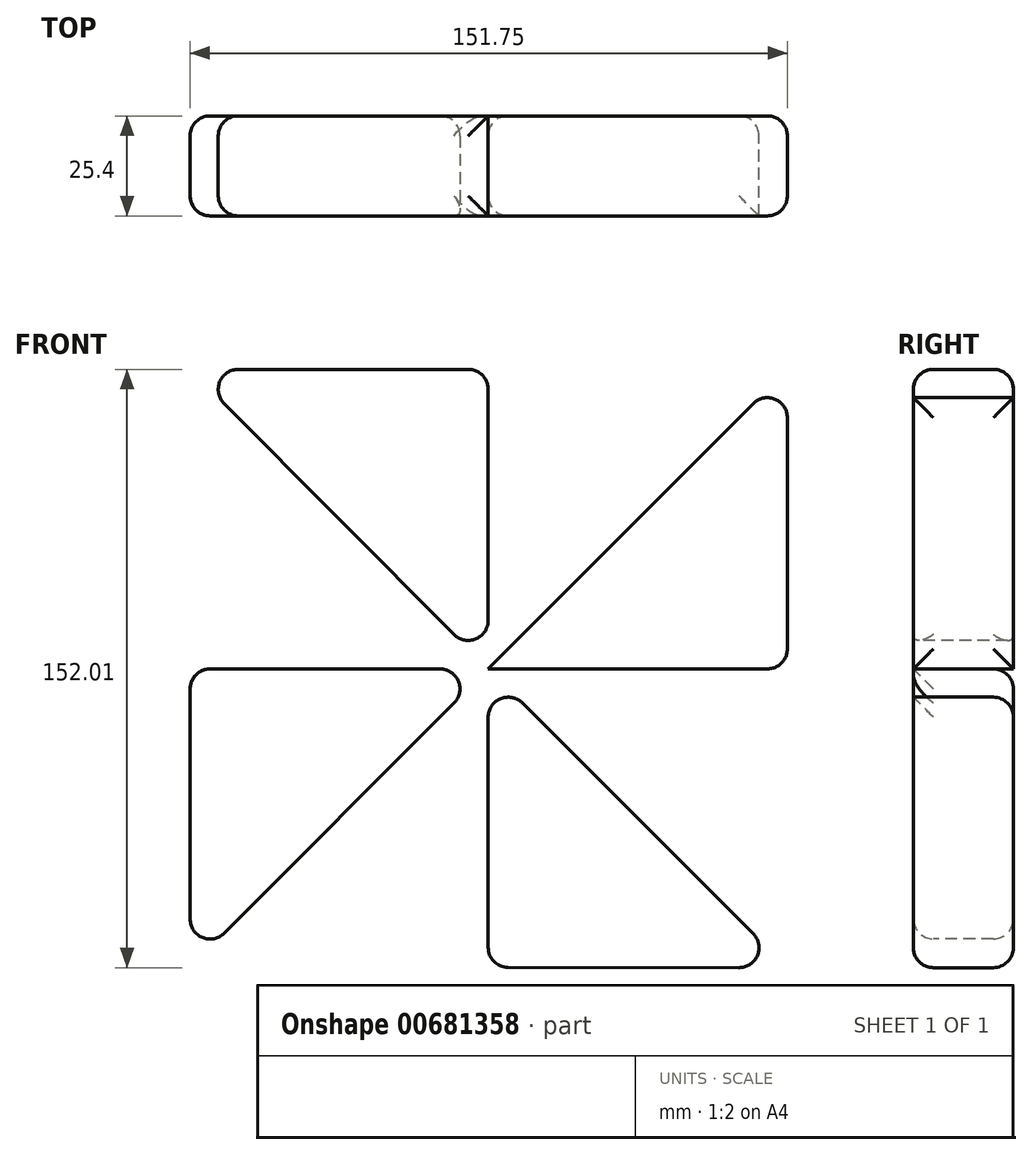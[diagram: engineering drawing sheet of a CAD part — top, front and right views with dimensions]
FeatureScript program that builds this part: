
annotation { "Feature Type Name" : "Feature", "Feature Type Description" : "" }
export const myFeature = defineFeature(function(context is Context, id is Id, definition is map)
    precondition{}
    {
        {
            var Q0;
            Q0=qCreatedBy(makeId("Front.planeOp"),FACE);
            var sketch = newSketch(context, id + "F0", { "sketchPlane" : qUnion([Q0])});
            skLineSegment(sketch, "E0", {"start": v(0, 0) * mm, "end": v(76.02, 76.11) * mm});
            skLineSegment(sketch, "E1", {"start": v(76.02, 76.11) * mm, "end": v(-75.73, -75.83) * mm});
            skLineSegment(sketch, "E2", {"start": v(-75.73, -75.83) * mm, "end": v(0, -75.83) * mm});
            skLineSegment(sketch, "E3", {"start": v(0, -75.83) * mm, "end": v(0, 0) * mm});
            skLineSegment(sketch, "E4", {"start": v(0, 76.11) * mm, "end": v(-75.71, 76.11) * mm});
            skLineSegment(sketch, "E5", {"start": v(-75.71, 76.11) * mm, "end": v(0, 0) * mm});
            skLineSegment(sketch, "E6", {"start": v(0, 0) * mm, "end": v(76.02, -75.92) * mm});
            skLineSegment(sketch, "E7", {"start": v(76.02, -75.92) * mm, "end": v(0, -75.83) * mm});
            skLineSegment(sketch, "E8", {"start": v(0, 76.11) * mm, "end": v(0, 0) * mm});
            skLineSegment(sketch, "E9", {"start": v(0, 76.11) * mm, "end": v(76.02, 76.11) * mm});
            skLineSegment(sketch, "E10", {"start": v(0, 0) * mm, "end": v(76.02, 0) * mm});
            skLineSegment(sketch, "E11", {"start": v(76.02, 0) * mm, "end": v(-75.71, 0) * mm});
            skLineSegment(sketch, "E12", {"start": v(-75.71, 0) * mm, "end": v(-75.73, -75.83) * mm});
            skLineSegment(sketch, "E13", {"start": v(76.02, 0) * mm, "end": v(76.02, -75.92) * mm});
            skLineSegment(sketch, "E14", {"start": v(76.02, 76.11) * mm, "end": v(76.02, 0) * mm});
            skLineSegment(sketch, "E15", {"start": v(-75.71, 76.11) * mm, "end": v(-75.71, 0) * mm});
            skSolve(sketch);
        }
        {
            var Q0;
            Q0=makeQuery(id+"F0.imprint","IMPRINT",FACE,{"disambiguationData":[TD([[makeQuery(id+"F0.imprint","IMPRINT",EDGE,{"derivedFrom":sQuery(id+"F0.wireOp",EDGE,"E3")}),-1.0]])]});
            var Q1;
            Q1=makeQuery(id+"F0.imprint","IMPRINT",FACE,{"disambiguationData":[TD([[makeQuery(id+"F0.imprint","IMPRINT",EDGE,{"derivedFrom":sQuery(id+"F0.wireOp",EDGE,"E4")}),1.0]])]});
            var Q2;
            {var subQ0=sQuery(id+"F0.wireOp",EDGE,"E14");Q2=makeQuery(id+"F0.imprint","IMPRINT",FACE,{"disambiguationData":[TD([[makeQuery(id+"F0.imprint","IMPRINT",EDGE,{"derivedFrom":subQ0}),-1.0]])]});}
            var Q3;
            {var subQ0=sQuery(id+"F0.wireOp",EDGE,"E12");Q3=makeQuery(id+"F0.imprint","IMPRINT",FACE,{"disambiguationData":[TD([[makeQuery(id+"F0.imprint","IMPRINT",EDGE,{"derivedFrom":subQ0}),1.0]])]});}
            extrude(context, id + "F1", {"entities" : qUnion([Q0, Q1, Q2, Q3]), "depth" : 25.4 * mm, "offsetDistance" : 25.4 * mm});
        }
        {
            var Q0;
            Q0=makeQuery(id+"F1.opExtrude","SWEPT_FACE",FACE,{"disambiguationData":[OSD([sQuery(id+"F0.wireOp",EDGE,"E5")])]});
            var Q1;
            Q1=makeQuery(id+"F1.opExtrude","SWEPT_FACE",FACE,{"disambiguationData":[OSD([sQuery(id+"F0.wireOp",EDGE,"E4")])]});
            var Q2;
            Q2=makeQuery(id+"F1.opExtrude","SWEPT_FACE",FACE,{"disambiguationData":[OSD([sQuery(id+"F0.wireOp",EDGE,"E14")])]});
            var Q3;
            {var subQ0=sQuery(id+"F0.wireOp",EDGE,"E1");Q3=makeQuery(id+"F1.opExtrude","SWEPT_FACE",FACE,{"disambiguationData":[OSD([subQ0]),TDD([makeQuery(id+"F0.imprint","IMPRINT",EDGE,{"disambiguationData":[TD([[makeQuery(id+"F0.imprint","INTERSECT",VERTEX,{"derivedFrom":[subQ0,sQuery(id+"F0.wireOp",EDGE,"E9"),sQuery(id+"F0.wireOp",EDGE,"E14")]}),-1.0]])],"derivedFrom":subQ0})])]});}
            var Q4;
            Q4=makeQuery(id+"F1.opExtrude","SWEPT_FACE",FACE,{"disambiguationData":[OSD([sQuery(id+"F0.wireOp",EDGE,"E7")])]});
            var Q5;
            Q5=makeQuery(id+"F1.opExtrude","SWEPT_FACE",FACE,{"disambiguationData":[OSD([sQuery(id+"F0.wireOp",EDGE,"E3")])]});
            var Q6;
            {var subQ0=sQuery(id+"F0.wireOp",EDGE,"E1");Q6=makeQuery(id+"F1.opExtrude","SWEPT_FACE",FACE,{"disambiguationData":[OSD([subQ0]),TDD([makeQuery(id+"F0.imprint","IMPRINT",EDGE,{"disambiguationData":[TD([[makeQuery(id+"F0.imprint","INTERSECT",VERTEX,{"derivedFrom":[subQ0,sQuery(id+"F0.wireOp",EDGE,"E2"),sQuery(id+"F0.wireOp",EDGE,"E12")]}),1.0]])],"derivedFrom":subQ0})])]});}
            var Q7;
            Q7=makeQuery(id+"F1.opExtrude","SWEPT_EDGE",EDGE,{"disambiguationData":[OSD([sQuery(id+"F0.wireOp",EDGE,"E11"),sQuery(id+"F0.wireOp",EDGE,"E12"),sQuery(id+"F0.wireOp",EDGE,"E15")])]});
            var Q8;
            Q8=makeQuery(id+"F1.opExtrude","SWEPT_FACE",FACE,{"disambiguationData":[OSD([sQuery(id+"F0.wireOp",EDGE,"E12")])]});
            var Q9;
            Q9=makeQuery(id+"F1.opExtrude","SWEPT_EDGE",EDGE,{"disambiguationData":[OSD([sQuery(id+"F0.wireOp",EDGE,"E6"),sQuery(id+"F0.wireOp",EDGE,"E7"),sQuery(id+"F0.wireOp",EDGE,"E13")])]});
            var Q10;
            Q10=makeQuery(id+"F1.opExtrude","CAP_EDGE",EDGE,{"disambiguationData":[OSD([sQuery(id+"F0.wireOp",EDGE,"E6")])],"isStart":true});
            var Q11;
            Q11=makeQuery(id+"F1.opExtrude","CAP_EDGE",EDGE,{"disambiguationData":[OSD([sQuery(id+"F0.wireOp",EDGE,"E7")])],"isStart":true});
            var Q12;
            Q12=makeQuery(id+"F1.opExtrude","SWEPT_EDGE",EDGE,{"disambiguationData":[OSD([sQuery(id+"F0.wireOp",EDGE,"E11"),sQuery(id+"F0.wireOp",EDGE,"E13"),sQuery(id+"F0.wireOp",EDGE,"E14")])]});
            var Q13;
            {var subQ0=sQuery(id+"F0.wireOp",EDGE,"E11");Q13=makeQuery(id+"F1.opExtrude","CAP_EDGE",EDGE,{"disambiguationData":[OSD([subQ0]),TDD([makeQuery(id+"F0.imprint","IMPRINT",EDGE,{"disambiguationData":[TD([[makeQuery(id+"F0.imprint","INTERSECT",VERTEX,{"derivedFrom":[subQ0,sQuery(id+"F0.wireOp",EDGE,"E13"),sQuery(id+"F0.wireOp",EDGE,"E14")]}),-1.0]])],"derivedFrom":subQ0})])],"isStart":true});}
            var Q14;
            Q14=makeQuery(id+"F1.opExtrude","CAP_EDGE",EDGE,{"disambiguationData":[OSD([sQuery(id+"F0.wireOp",EDGE,"E14")])],"isStart":true});
            fillet(context, id + "F2", {"entities" : qUnion([Q0, Q1, Q2, Q3, Q4, Q5, Q6, Q7, Q8, Q9, Q10, Q11, Q12, Q13, Q14]), "radius" : 5.08 * mm, "tangentPropagation" : true, "allowEdgeOverflow" : false});
        }
    });
